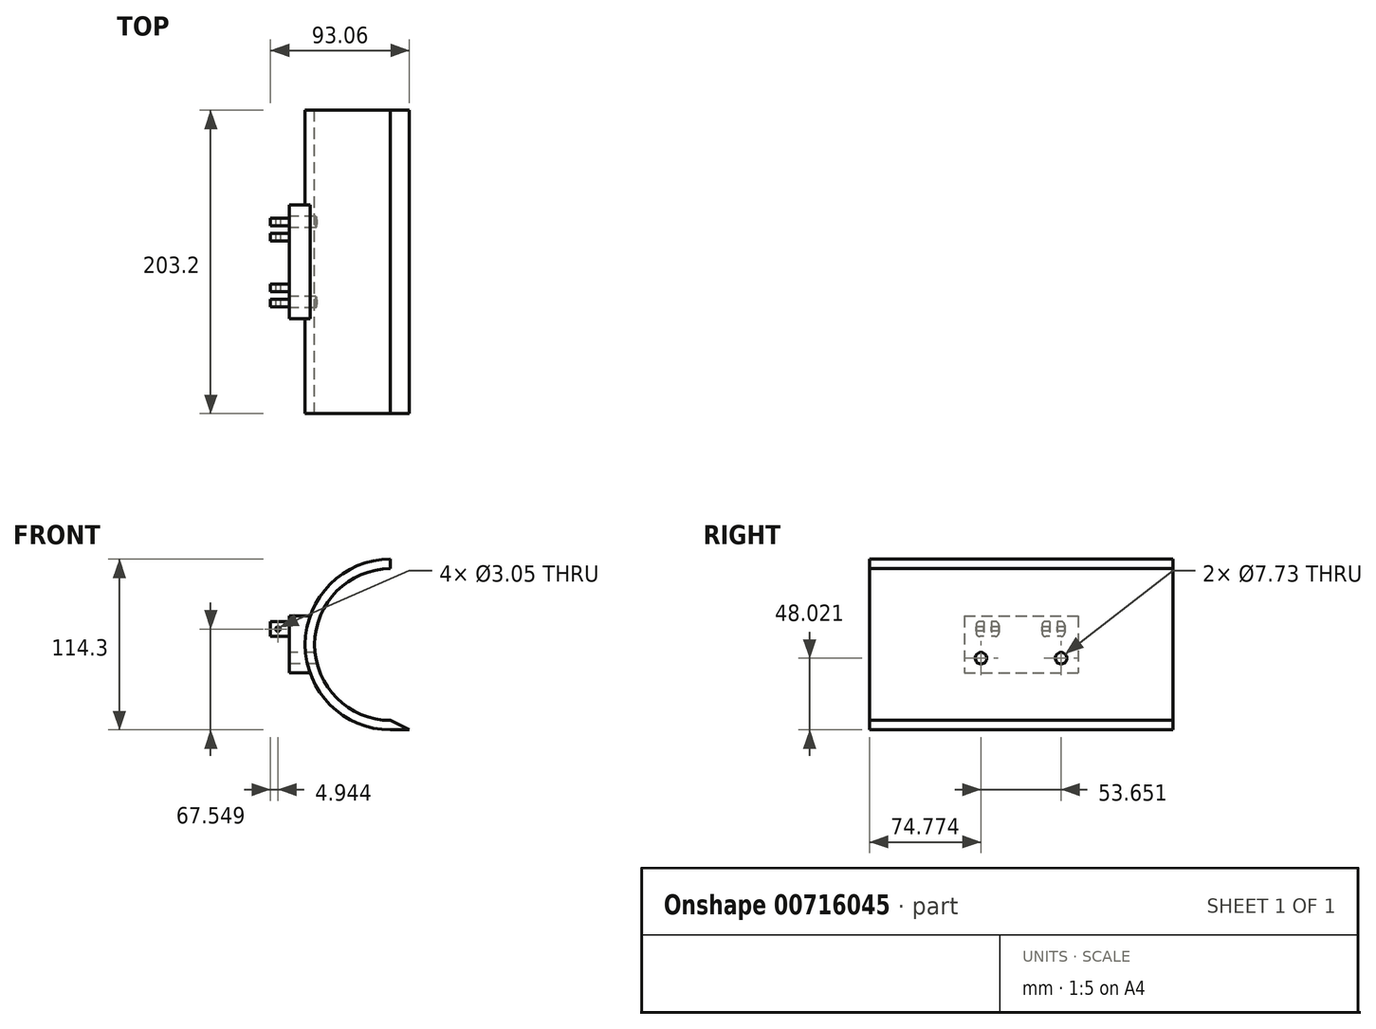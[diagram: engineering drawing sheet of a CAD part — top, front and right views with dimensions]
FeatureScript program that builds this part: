
annotation { "Feature Type Name" : "Feature", "Feature Type Description" : "" }
export const myFeature = defineFeature(function(context is Context, id is Id, definition is map)
    precondition{}
    {
        {
            var Q0;
            Q0=qCreatedBy(makeId("Front.planeOp"),FACE);
            var sketch = newSketch(context, id + "F0", { "sketchPlane" : qUnion([Q0])});
            skArc(sketch, "E0", {"start": v(0, 50.8) * mm, "mid": v(-50.8, 0) * mm, "end": v(0, -50.8) * mm});
            skArc(sketch, "E1", {"start": v(0, 57.15) * mm, "mid": v(-57.15, 0) * mm, "end": v(0, -57.15) * mm});
            skLineSegment(sketch, "E2", {"start": v(0, 50.8) * mm, "end": v(0, 57.15) * mm});
            skLineSegment(sketch, "E3", {"start": v(0, -57.15) * mm, "end": v(12.7, -57.15) * mm});
            skLineSegment(sketch, "E4", {"start": v(12.7, -57.15) * mm, "end": v(0, -50.8) * mm});
            skLineSegment(sketch, "E5", {"start": v(-53.88, 19.05) * mm, "end": v(-67.66, 19.05) * mm});
            skLineSegment(sketch, "E6", {"start": v(-67.66, 19.05) * mm, "end": v(-67.66, -19.05) * mm});
            skLineSegment(sketch, "E7", {"start": v(-67.66, -19.05) * mm, "end": v(-53.88, -19.05) * mm});
            skLineSegment(sketch, "E8", {"start": v(-63.26, 0) * mm, "end": v(-63.26, 19.05) * mm, "construction": true});
            skLineSegment(sketch, "E9", {"start": v(-63.26, -19.05) * mm, "end": v(-63.26, 0) * mm, "construction": true});
            skSolve(sketch);
        }
        {
            var Q0;
            Q0=makeQuery(id+"F0.imprint","IMPRINT",FACE,{"disambiguationData":[TD([[makeQuery(id+"F0.imprint","IMPRINT",EDGE,{"derivedFrom":sQuery(id+"F0.wireOp",EDGE,"E0")}),-1.0]])]});
            extrude(context, id + "F1", {"entities" : qUnion([Q0]), "endBound" : BoundingType.SYMMETRIC, "depth" : 203.2 * mm, "offsetDistance" : 25.4 * mm});
        }
        {
            var Q0;
            {var subQ0=sQuery(id+"F0.wireOp",EDGE,"E5");Q0=makeQuery(id+"F0.imprint","IMPRINT",FACE,{"disambiguationData":[TD([[makeQuery(id+"F0.imprint","IMPRINT",EDGE,{"derivedFrom":subQ0}),1.0]])]});}
            extrude(context, id + "F2", {"entities" : qUnion([Q0]), "operationType" : NewBodyOperationType.ADD, "endBound" : BoundingType.SYMMETRIC, "depth" : 76.2 * mm, "offsetDistance" : 25.4 * mm});
        }
        {
            var Q0;
            Q0=makeQuery(id+"F2.opExtrude","SWEPT_FACE",FACE,{"disambiguationData":[OSD([sQuery(id+"F0.wireOp",EDGE,"E6")])]});
            var sketch = newSketch(context, id + "F3", { "sketchPlane" : qUnion([Q0])});
            skCircle(sketch, "E10", {"center": v(-26.83, -9.13) * mm, "radius": 3.86 * mm});
            skCircle(sketch, "E11", {"center": v(26.83, -9.13) * mm, "radius": 3.86 * mm});
            skLineSegment(sketch, "E12", {"start": v(-38.1, 0) * mm, "end": v(38.1, 0) * mm, "construction": true});
            skLineSegment(sketch, "E13", {"start": v(0, -19.05) * mm, "end": v(0, 19.05) * mm, "construction": true});
            skLineSegment(sketch, "E14", {"start": v(26.83, -9.13) * mm, "end": v(26.83, 0) * mm, "construction": true});
            skLineSegment(sketch, "E15", {"start": v(26.83, -9.13) * mm, "end": v(0, -9.13) * mm, "construction": true});
            skLineSegment(sketch, "E16", {"start": v(0, -9.13) * mm, "end": v(-26.83, -9.13) * mm, "construction": true});
            skLineSegment(sketch, "E17", {"start": v(-26.83, 0) * mm, "end": v(-26.83, -9.13) * mm, "construction": true});
            skLineSegment(sketch, "E18.bottom", {"start": v(-29.21, 15.42) * mm, "end": v(-24.13, 15.42) * mm});
            skLineSegment(sketch, "E18.top", {"start": v(-29.21, 5.37) * mm, "end": v(-24.13, 5.37) * mm});
            skLineSegment(sketch, "E18.left", {"start": v(-29.21, 15.42) * mm, "end": v(-29.21, 5.37) * mm});
            skLineSegment(sketch, "E18.right", {"start": v(-24.13, 15.42) * mm, "end": v(-24.13, 5.37) * mm});
            skLineSegment(sketch, "E19.bottom", {"start": v(-19.05, 15.42) * mm, "end": v(-13.97, 15.42) * mm});
            skLineSegment(sketch, "E19.top", {"start": v(-19.05, 5.37) * mm, "end": v(-13.97, 5.37) * mm});
            skLineSegment(sketch, "E19.left", {"start": v(-19.05, 15.42) * mm, "end": v(-19.05, 5.37) * mm});
            skLineSegment(sketch, "E19.right", {"start": v(-13.97, 15.42) * mm, "end": v(-13.97, 5.37) * mm});
            skLineSegment(sketch, "E20.bottom", {"start": v(14.89, 15.42) * mm, "end": v(19.97, 15.42) * mm});
            skLineSegment(sketch, "E20.top", {"start": v(14.89, 5.37) * mm, "end": v(19.97, 5.37) * mm});
            skLineSegment(sketch, "E20.left", {"start": v(14.89, 15.42) * mm, "end": v(14.89, 5.37) * mm});
            skLineSegment(sketch, "E20.right", {"start": v(19.97, 15.42) * mm, "end": v(19.97, 5.37) * mm});
            skLineSegment(sketch, "E21.bottom", {"start": v(25.05, 15.42) * mm, "end": v(30.13, 15.42) * mm});
            skLineSegment(sketch, "E21.top", {"start": v(25.05, 5.37) * mm, "end": v(30.13, 5.37) * mm});
            skLineSegment(sketch, "E21.left", {"start": v(25.05, 15.42) * mm, "end": v(25.05, 5.37) * mm});
            skLineSegment(sketch, "E21.right", {"start": v(30.13, 15.42) * mm, "end": v(30.13, 5.37) * mm});
            skLineSegment(sketch, "E22", {"start": v(-38.1, 15.42) * mm, "end": v(38.1, 15.42) * mm, "construction": true});
            skPoint(sketch, "E22.endSnap0", {"position": v(-16.51, 15.42) * mm});
            skLineSegment(sketch, "E23", {"start": v(-19.05, 5.37) * mm, "end": v(-24.13, 5.37) * mm, "construction": true});
            skLineSegment(sketch, "E24", {"start": v(19.97, 5.37) * mm, "end": v(25.05, 5.37) * mm, "construction": true});
            skSolve(sketch);
        }
        {
            var Q0;
            Q0=makeQuery(id+"F3.imprint","IMPRINT",FACE,{"disambiguationData":[TD([[makeQuery(id+"F3.imprint","IMPRINT",EDGE,{"derivedFrom":sQuery(id+"F3.wireOp",EDGE,"E10")}),1.0]])]});
            var Q1;
            Q1=makeQuery(id+"F3.imprint","IMPRINT",FACE,{"disambiguationData":[TD([[makeQuery(id+"F3.imprint","IMPRINT",EDGE,{"derivedFrom":sQuery(id+"F3.wireOp",EDGE,"E11")}),1.0]])]});
            extrude(context, id + "F4", {"entities" : qUnion([Q0, Q1]), "operationType" : NewBodyOperationType.REMOVE, "oppositeDirection" : true, "depth" : 25.4 * mm, "offsetDistance" : 25.4 * mm});
        }
        {
            var Q0;
            Q0=makeQuery(id+"F3.imprint","IMPRINT",FACE,{"disambiguationData":[TD([[makeQuery(id+"F3.imprint","IMPRINT",EDGE,{"derivedFrom":sQuery(id+"F3.wireOp",EDGE,"E18.bottom")}),-1.0]])]});
            var Q1;
            Q1=makeQuery(id+"F3.imprint","IMPRINT",FACE,{"disambiguationData":[TD([[makeQuery(id+"F3.imprint","IMPRINT",EDGE,{"derivedFrom":sQuery(id+"F3.wireOp",EDGE,"E19.bottom")}),-1.0]])]});
            var Q2;
            Q2=makeQuery(id+"F3.imprint","IMPRINT",FACE,{"disambiguationData":[TD([[makeQuery(id+"F3.imprint","IMPRINT",EDGE,{"derivedFrom":sQuery(id+"F3.wireOp",EDGE,"E20.bottom")}),-1.0]])]});
            var Q3;
            Q3=makeQuery(id+"F3.imprint","IMPRINT",FACE,{"disambiguationData":[TD([[makeQuery(id+"F3.imprint","IMPRINT",EDGE,{"derivedFrom":sQuery(id+"F3.wireOp",EDGE,"E21.bottom")}),-1.0]])]});
            extrude(context, id + "F5", {"entities" : qUnion([Q0, Q1, Q2, Q3]), "operationType" : NewBodyOperationType.ADD, "depth" : 12.7 * mm, "offsetDistance" : 25.4 * mm});
        }
        {
            var Q0;
            Q0=makeQuery(id+"F5.opExtrude","SWEPT_EDGE",EDGE,{"disambiguationData":[OSD([sQuery(id+"F3.wireOp",EDGE,"E18.bottom"),sQuery(id+"F3.wireOp",EDGE,"E18.left")])]});
            var Q1;
            Q1=makeQuery(id+"F5.opExtrude","SWEPT_EDGE",EDGE,{"disambiguationData":[OSD([sQuery(id+"F3.wireOp",EDGE,"E18.top"),sQuery(id+"F3.wireOp",EDGE,"E18.left")])]});
            var Q2;
            Q2=makeQuery(id+"F5.opExtrude","SWEPT_EDGE",EDGE,{"disambiguationData":[OSD([sQuery(id+"F3.wireOp",EDGE,"E19.top"),sQuery(id+"F3.wireOp",EDGE,"E19.right")])]});
            var Q3;
            Q3=makeQuery(id+"F5.opExtrude","SWEPT_EDGE",EDGE,{"disambiguationData":[OSD([sQuery(id+"F3.wireOp",EDGE,"E19.bottom"),sQuery(id+"F3.wireOp",EDGE,"E19.right")])]});
            var Q4;
            Q4=makeQuery(id+"F5.opExtrude","SWEPT_EDGE",EDGE,{"disambiguationData":[OSD([sQuery(id+"F3.wireOp",EDGE,"E20.top"),sQuery(id+"F3.wireOp",EDGE,"E20.left")])]});
            var Q5;
            Q5=makeQuery(id+"F5.opExtrude","SWEPT_EDGE",EDGE,{"disambiguationData":[OSD([sQuery(id+"F3.wireOp",EDGE,"E21.top"),sQuery(id+"F3.wireOp",EDGE,"E21.right")])]});
            var Q6;
            Q6=makeQuery(id+"F5.opExtrude","SWEPT_EDGE",EDGE,{"disambiguationData":[OSD([sQuery(id+"F3.wireOp",EDGE,"E21.bottom"),sQuery(id+"F3.wireOp",EDGE,"E21.right")])]});
            var Q7;
            Q7=makeQuery(id+"F5.opExtrude","SWEPT_EDGE",EDGE,{"disambiguationData":[OSD([sQuery(id+"F3.wireOp",EDGE,"E20.bottom"),sQuery(id+"F3.wireOp",EDGE,"E20.left")])]});
            fillet(context, id + "F6", {"entities" : qUnion([Q0, Q1, Q2, Q3, Q4, Q5, Q6, Q7]), "radius" : 2.54 * mm, "tangentPropagation" : true, "allowEdgeOverflow" : false});
        }
        {
            var Q0;
            Q0=makeQuery(id+"F5.opExtrude","SWEPT_FACE",FACE,{"disambiguationData":[OSD([sQuery(id+"F3.wireOp",EDGE,"E21.right")])]});
            var sketch = newSketch(context, id + "F7", { "sketchPlane" : qUnion([Q0])});
            skCircle(sketch, "E25", {"center": v(-75.42, 10.4) * mm, "radius": 1.52 * mm});
            skLineSegment(sketch, "E26", {"start": v(-67.66, 10.4) * mm, "end": v(-80.36, 10.4) * mm, "construction": true});
            skSolve(sketch);
        }
        {
            var Q0;
            Q0 = qSketchRegion(id + "F7", true);
            extrude(context, id + "F8", {"entities" : qUnion([Q0]), "operationType" : NewBodyOperationType.REMOVE, "oppositeDirection" : true, "depth" : 101.6 * mm, "offsetDistance" : 25.4 * mm});
        }
    });
